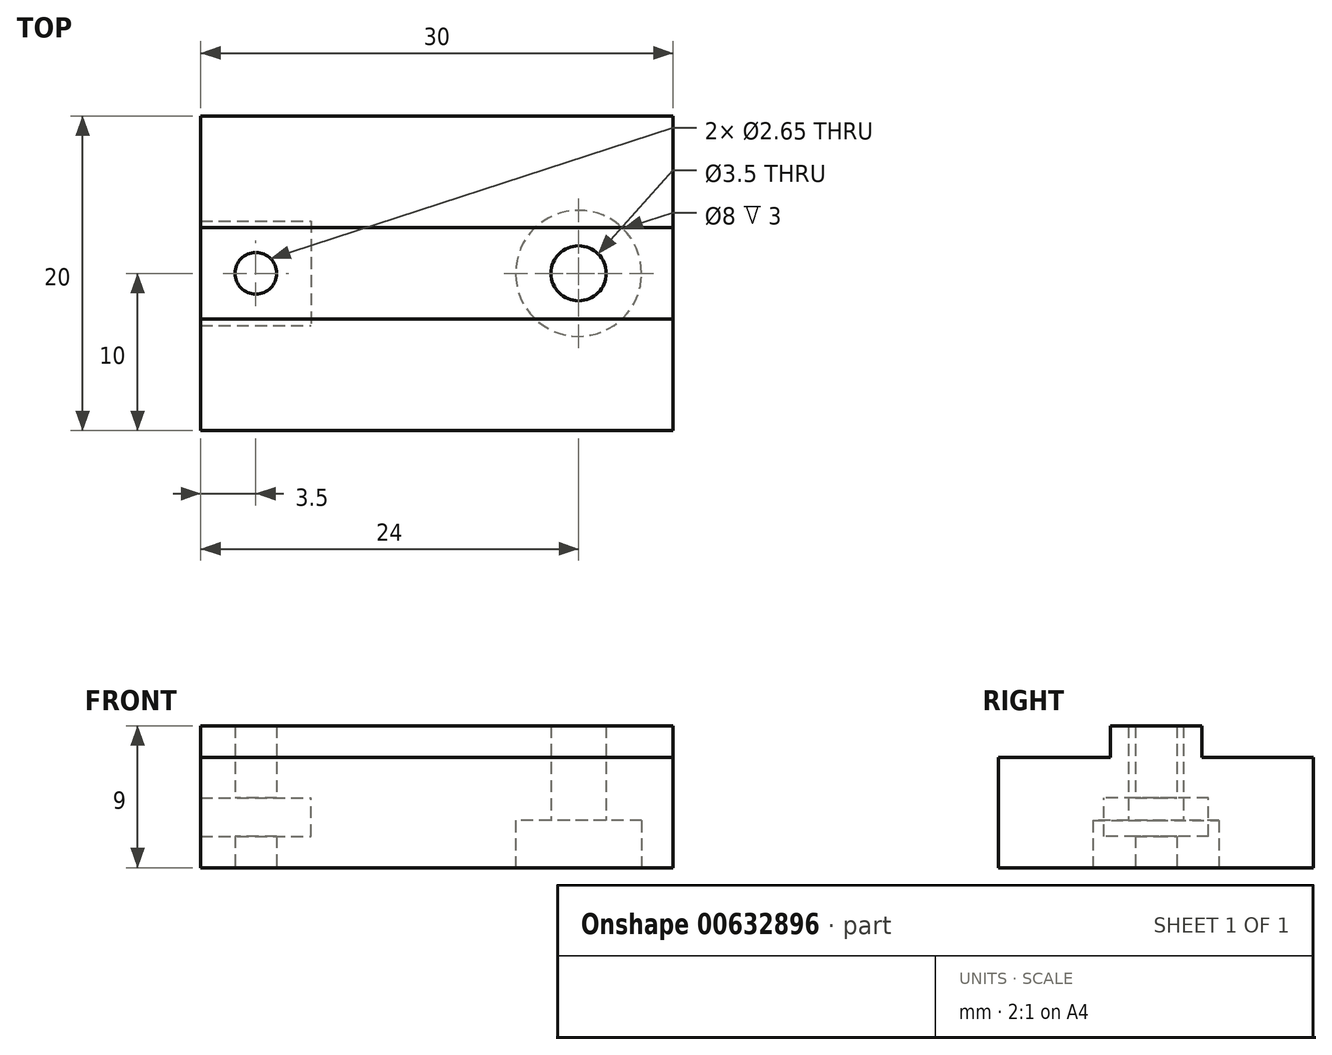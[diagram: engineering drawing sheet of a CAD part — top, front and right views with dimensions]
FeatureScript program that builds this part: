
annotation { "Feature Type Name" : "Feature", "Feature Type Description" : "" }
export const myFeature = defineFeature(function(context is Context, id is Id, definition is map)
    precondition{}
    {
        {
            var Q0;
            Q0=qCreatedBy(makeId("Top.planeOp"),FACE);
            var sketch = newSketch(context, id + "F0", { "sketchPlane" : qUnion([Q0])});
            skLineSegment(sketch, "E0.bottom", {"start": v(15, -10) * mm, "end": v(-15, -10) * mm});
            skLineSegment(sketch, "E0.top", {"start": v(15, 10) * mm, "end": v(-15, 10) * mm});
            skLineSegment(sketch, "E0.left", {"start": v(15, -10) * mm, "end": v(15, 10) * mm});
            skLineSegment(sketch, "E0.right", {"start": v(-15, -10) * mm, "end": v(-15, 10) * mm});
            skPoint(sketch, "E0.middle", {"position": v(0, 0) * mm});
            skLineSegment(sketch, "E1", {"start": v(-15, 0) * mm, "end": v(15, 0) * mm});
            skLineSegment(sketch, "E2.0", {"start": v(-15, -2.9) * mm, "end": v(15, -2.9) * mm});
            skLineSegment(sketch, "E3.0", {"start": v(-15, 2.9) * mm, "end": v(15, 2.9) * mm});
            skSolve(sketch);
        }
        {
            var Q0;
            {var subQ0=sQuery(id+"F0.wireOp",EDGE,"E1");Q0=makeQuery(id+"F0.imprint","IMPRINT",FACE,{"disambiguationData":[TD([[makeQuery(id+"F0.imprint","IMPRINT",EDGE,{"derivedFrom":subQ0}),-1.0]])]});}
            var Q1;
            {var subQ0=sQuery(id+"F0.wireOp",EDGE,"E0.bottom");Q1=makeQuery(id+"F0.imprint","IMPRINT",FACE,{"disambiguationData":[TD([[makeQuery(id+"F0.imprint","IMPRINT",EDGE,{"derivedFrom":subQ0}),-1.0]])]});}
            var Q2;
            {var subQ0=sQuery(id+"F0.wireOp",EDGE,"E0.top");Q2=makeQuery(id+"F0.imprint","IMPRINT",FACE,{"disambiguationData":[TD([[makeQuery(id+"F0.imprint","IMPRINT",EDGE,{"derivedFrom":subQ0}),1.0]])]});}
            var Q3;
            {var subQ0=sQuery(id+"F0.wireOp",EDGE,"E1");Q3=makeQuery(id+"F0.imprint","IMPRINT",FACE,{"disambiguationData":[TD([[makeQuery(id+"F0.imprint","IMPRINT",EDGE,{"derivedFrom":subQ0}),1.0]])]});}
            extrude(context, id + "F1", {"entities" : qUnion([Q0, Q1, Q2, Q3]), "depth" : 7 * mm, "offsetDistance" : 25 * mm});
        }
        {
            var Q0;
            {var subQ0=sQuery(id+"F0.wireOp",EDGE,"E1");Q0=makeQuery(id+"F0.imprint","IMPRINT",FACE,{"disambiguationData":[TD([[makeQuery(id+"F0.imprint","IMPRINT",EDGE,{"derivedFrom":subQ0}),-1.0]])]});}
            var Q1;
            {var subQ0=sQuery(id+"F0.wireOp",EDGE,"E1");Q1=makeQuery(id+"F0.imprint","IMPRINT",FACE,{"disambiguationData":[TD([[makeQuery(id+"F0.imprint","IMPRINT",EDGE,{"derivedFrom":subQ0}),1.0]])]});}
            extrude(context, id + "F2", {"entities" : qUnion([Q0, Q1]), "operationType" : NewBodyOperationType.ADD, "depth" : 9 * mm, "offsetDistance" : 25 * mm});
        }
        {
            var Q0;
            Q0=qCreatedBy(makeId("Top.planeOp"),FACE);
            var sketch = newSketch(context, id + "F3", { "sketchPlane" : qUnion([Q0])});
            skCircle(sketch, "E4", {"center": v(9, 0) * mm, "radius": 1.75 * mm});
            skCircle(sketch, "E5", {"center": v(9, 0) * mm, "radius": 4 * mm});
            skSolve(sketch);
        }
        {
            var Q0;
            Q0=makeQuery(id+"F3.imprint","IMPRINT",FACE,{"disambiguationData":[TD([[makeQuery(id+"F3.imprint","IMPRINT",EDGE,{"derivedFrom":sQuery(id+"F3.wireOp",EDGE,"E4")}),1.0]])]});
            extrude(context, id + "F4", {"entities" : qUnion([Q0]), "operationType" : NewBodyOperationType.REMOVE, "depth" : 10 * mm, "offsetDistance" : 25 * mm});
        }
        {
            var Q0;
            Q0=makeQuery(id+"F3.imprint","IMPRINT",FACE,{"disambiguationData":[TD([[makeQuery(id+"F3.imprint","IMPRINT",EDGE,{"derivedFrom":sQuery(id+"F3.wireOp",EDGE,"E4")}),-1.0]])]});
            extrude(context, id + "F5", {"entities" : qUnion([Q0]), "operationType" : NewBodyOperationType.REMOVE, "depth" : 3 * mm, "offsetDistance" : 25 * mm});
        }
        {
            var Q0;
            Q0=qCreatedBy(makeId("Right.planeOp"),FACE);
            var sketch = newSketch(context, id + "F6", { "sketchPlane" : qUnion([Q0])});
            skLineSegment(sketch, "E6.bottom", {"start": v(3.32, 2) * mm, "end": v(-3.33, 2) * mm});
            skLineSegment(sketch, "E6.top", {"start": v(3.33, 4.42) * mm, "end": v(-3.32, 4.42) * mm});
            skLineSegment(sketch, "E6.left", {"start": v(3.32, 2) * mm, "end": v(3.33, 4.42) * mm});
            skLineSegment(sketch, "E6.right", {"start": v(-3.33, 2) * mm, "end": v(-3.32, 4.42) * mm});
            skPoint(sketch, "E6.middle", {"position": v(0, 3.2) * mm});
            skSolve(sketch);
        }
        {
            var Q0;
            Q0=makeQuery(id+"F6.imprint","IMPRINT",FACE,{"disambiguationData":[TD([[makeQuery(id+"F6.imprint","IMPRINT",EDGE,{"derivedFrom":sQuery(id+"F6.wireOp",EDGE,"E6.bottom")}),-1.0]])]});
            extrude(context, id + "F7", {"entities" : qUnion([Q0]), "operationType" : NewBodyOperationType.REMOVE, "oppositeDirection" : true, "depth" : 15 * mm, "offsetDistance" : 25 * mm, "hasSecondDirection" : true, "secondDirectionOppositeDirection" : true, "secondDirectionDepth" : 8 * mm});
        }
        {
            var Q0;
            Q0=qCreatedBy(makeId("Top.planeOp"),FACE);
            var sketch = newSketch(context, id + "F8", { "sketchPlane" : qUnion([Q0])});
            skCircle(sketch, "E7", {"center": v(-11.5, 0) * mm, "radius": 1.32 * mm});
            skSolve(sketch);
        }
        {
            var Q0;
            Q0=makeQuery(id+"F8.imprint","IMPRINT",FACE,{"disambiguationData":[TD([[makeQuery(id+"F8.imprint","IMPRINT",EDGE,{"derivedFrom":sQuery(id+"F8.wireOp",EDGE,"E7")}),1.0]])]});
            extrude(context, id + "F9", {"entities" : qUnion([Q0]), "operationType" : NewBodyOperationType.REMOVE, "depth" : 25 * mm, "offsetDistance" : 25 * mm});
        }
    });
